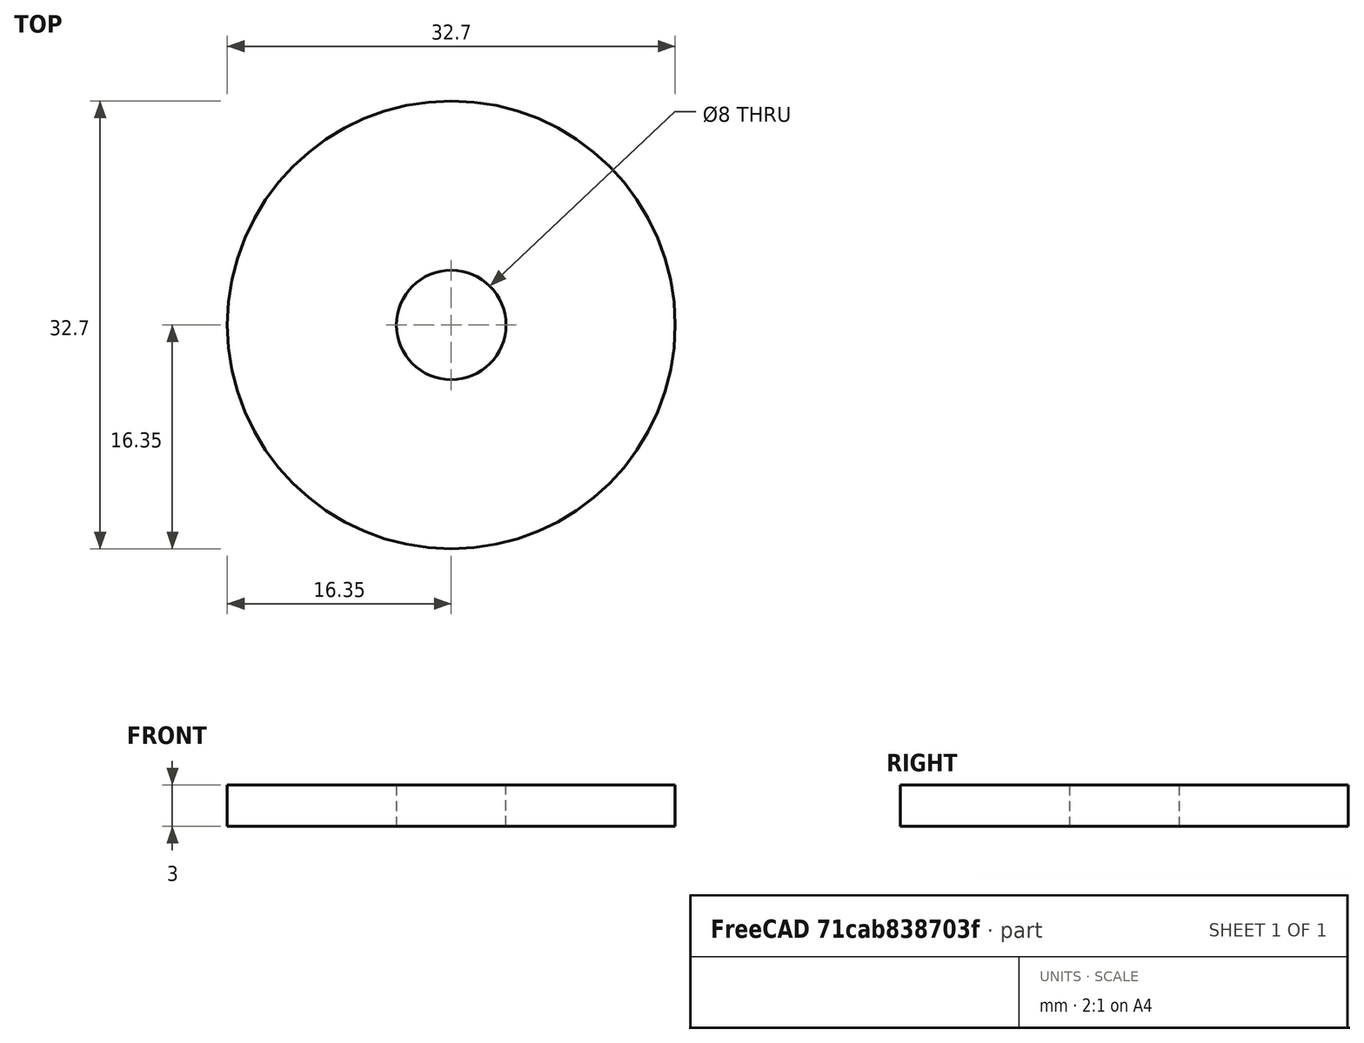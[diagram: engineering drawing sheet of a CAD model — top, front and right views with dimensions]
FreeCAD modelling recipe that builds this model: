
FCSTD DOCUMENT  (FreeCAD 0.18R4 (GitTag))
Label: Tapa potenciometro
License: All rights reserved
LicenseURL: http://en.wikipedia.org/wiki/All_rights_reserved
objects: PartDesign::Body×2, Sketcher::SketchObject×1, PartDesign::Pad×1
note: 5 computed .brp shape members not serialized (recipe doc carries the construction recipe); baked Part::Feature solids carry a one-line shape summary decoded from their .brp

FEATURE [PartDesign::Body] Body
  Origin = -> Origin
FEATURE [Sketcher::SketchObject] Sketch
  MapMode = 5
  Support = -> [XY_Plane001]
  sketch-geometry (2):
    g0: Circle CenterX=0 CenterY=0 CenterZ=0 NormalX=0 NormalY=0 NormalZ=1 AngleXU=0 Radius=16.35
    g1: Circle CenterX=0 CenterY=0 CenterZ=0 NormalX=0 NormalY=0 NormalZ=1 AngleXU=0 Radius=4
  constraints (2):
    c: Radius(g0) = 16.35
    c: Radius(g1) = 4
FEATURE [PartDesign::Pad] Pad
  Length = 3
  Length2 = 100
  Profile = -> Sketch
  Type = 0
FEATURE [PartDesign::Body] Body001
  Group = -> [Sketch,Pad]
  Origin = -> Origin001
  Tip = -> Pad
